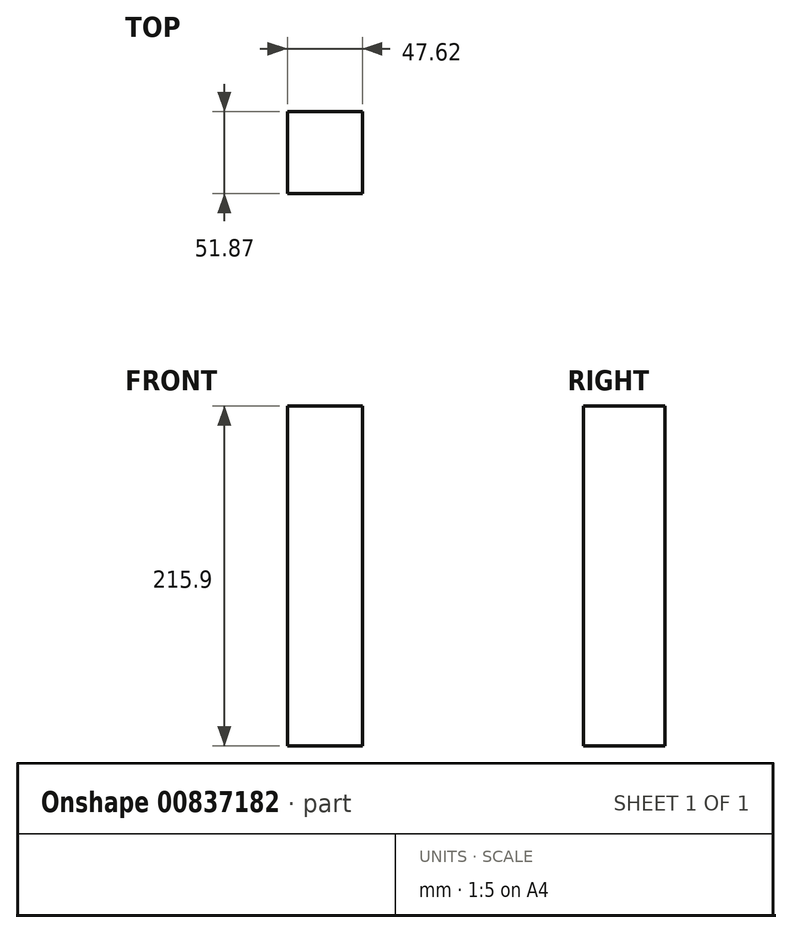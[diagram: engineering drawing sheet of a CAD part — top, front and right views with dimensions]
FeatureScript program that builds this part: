
annotation { "Feature Type Name" : "Feature", "Feature Type Description" : "" }
export const myFeature = defineFeature(function(context is Context, id is Id, definition is map)
    precondition{}
    {
        {
            var Q0;
            Q0=qCreatedBy(makeId("Top.planeOp"),FACE);
            var sketch = newSketch(context, id + "F0", { "sketchPlane" : qUnion([Q0])});
            skLineSegment(sketch, "E0.bottom", {"start": v(0, 0) * mm, "end": v(98.43, 0) * mm});
            skLineSegment(sketch, "E0.top", {"start": v(0, 98.43) * mm, "end": v(98.42, 98.43) * mm});
            skLineSegment(sketch, "E0.left", {"start": v(0, 0) * mm, "end": v(0, 98.43) * mm});
            skLineSegment(sketch, "E0.right", {"start": v(98.43, 0) * mm, "end": v(98.42, 98.42) * mm});
            skLineSegment(sketch, "E1.bottom", {"start": v(0, 0) * mm, "end": v(47.62, 0) * mm});
            skLineSegment(sketch, "E1.top", {"start": v(0, 51.87) * mm, "end": v(47.62, 51.87) * mm});
            skLineSegment(sketch, "E1.left", {"start": v(0, 0) * mm, "end": v(0, 51.87) * mm});
            skLineSegment(sketch, "E1.right", {"start": v(47.62, 0) * mm, "end": v(47.62, 51.87) * mm});
            skSolve(sketch);
        }
        {
            var Q0;
            Q0=makeQuery(id+"F0.imprint","IMPRINT",FACE,{"disambiguationData":[TD([[makeQuery(id+"F0.imprint","IMPRINT",EDGE,{"derivedFrom":sQuery(id+"F0.wireOp",EDGE,"E0.bottom")}),1.0]])]});
            extrude(context, id + "F1", {"entities" : qUnion([Q0]), "depth" : 215.9 * mm, "offsetDistance" : 25.4 * mm});
        }
    });
